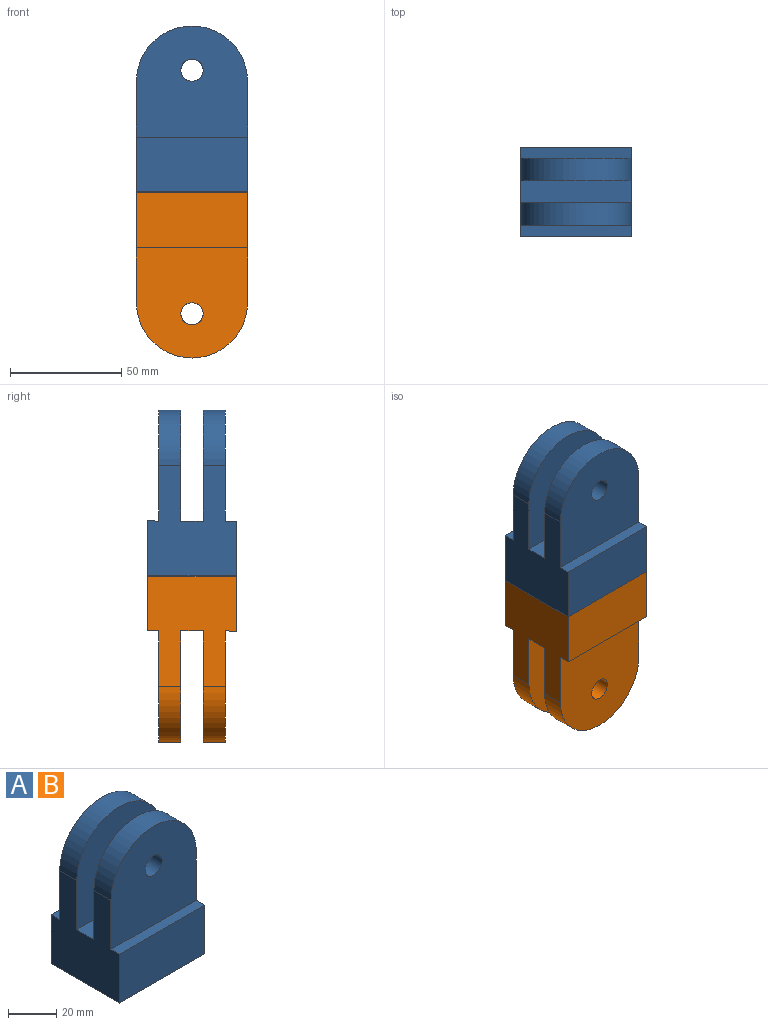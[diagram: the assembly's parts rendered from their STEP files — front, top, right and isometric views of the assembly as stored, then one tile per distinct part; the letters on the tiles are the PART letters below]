
ASSEMBLY  parts=2 mates=1
PART A: 26 faces, bbox 50x40x74.7 mm
  f0: plane 50x24.7mm, normal (0,-1,0), area 1235.2mm2, adj f2,f3,f4,f24
  f1: plane 50x24.85mm, normal (0,1,0), area 1242.6mm2, adj f2,f3,f4,f25
  f2: plane 49.7x40mm, normal (1,0,0), area 1488.5mm2, adj f0,f1,f4,f5,f6,f7,f8,f9
  f3: plane 49.7x40mm, normal (-1,0,0), area 1488.5mm2, adj f0,f1,f4,f5,f6,f7,f8,f9
  f4: plane 50x40mm, normal (0,0,-1), area 1716.5mm2, adj f0,f1,f2,f3,f13,f14,f15,f16
  f5: cylinder r=25mm len=50mm, axis (0,1,0), area 785.4mm2, adj f2,f3,f7,f10
  f6: cylinder r=25mm len=50mm, axis (0,1,0), area 785.4mm2, adj f2,f3,f8,f9
  f7: plane 50x50mm, normal (0,-1,0), area 2153.2mm2, adj f2,f3,f5,f11,f23
  f8: plane 50x50mm, normal (0,1,0), area 2153.2mm2, adj f2,f3,f6,f12,f23
  f9: plane 50x50mm, normal (0,-1,0), area 2153.2mm2, adj f2,f3,f6,f12,f24
  f10: plane 50x50mm, normal (0,1,0), area 2153.2mm2, adj f2,f3,f5,f11,f25
  f11: cylinder r=5mm len=10mm, axis (0,-1,0), area 314.2mm2, adj f7,f10
  f12: cylinder r=5mm len=10mm, axis (0,-1,0), area 314.2mm2, adj f8,f9
  f13: plane 20x3.5mm, normal (-1,0,0), area 70mm2, adj f4,f14,f16,f17
  f14: plane 40.5x20mm, normal (0,1,0), area 810mm2, adj f4,f13,f15,f17
  f15: plane 20x3.5mm, normal (1,0,0), area 70mm2, adj f4,f14,f16,f17
  f16: plane 40.5x20mm, normal (0,-1,0), area 810mm2, adj f4,f13,f15,f17
  f17: plane 40.5x3.5mm, normal (0,0,-1), area 141.8mm2, adj f13,f14,f15,f16
  f18: plane 20x3.5mm, normal (-1,0,0), area 70mm2, adj f4,f19,f21,f22
  f19: plane 40.5x20mm, normal (0,1,0), area 810mm2, adj f4,f18,f20,f22
  f20: plane 20x3.5mm, normal (1,0,0), area 70mm2, adj f4,f19,f21,f22
  f21: plane 40.5x20mm, normal (0,-1,0), area 810mm2, adj f4,f18,f20,f22
  f22: plane 40.5x3.5mm, normal (0,0,-1), area 141.8mm2, adj f18,f19,f20,f21
  f23: plane 50x10mm, normal (0,0,1), area 500mm2, adj f2,f3,f7,f8
  f24: plane 50x5mm, normal (0,0,1), area 250mm2, adj f0,f2,f3,f9
  f25: plane 50x5mm, normal (0,-0.03,1), area 250.1mm2, adj f1,f2,f3,f10
PART B: same geometry as A
PLACE A t=(12.73,18.25,-26.15)mm
PLACE B rot(axis=(1,0,0),180deg) t=(12.73,-21.79,-75.86)mm
MATE fastened B.f4 <-> A.f4  axis (0,0,1) through (12.7,-1.77,-51)mm
